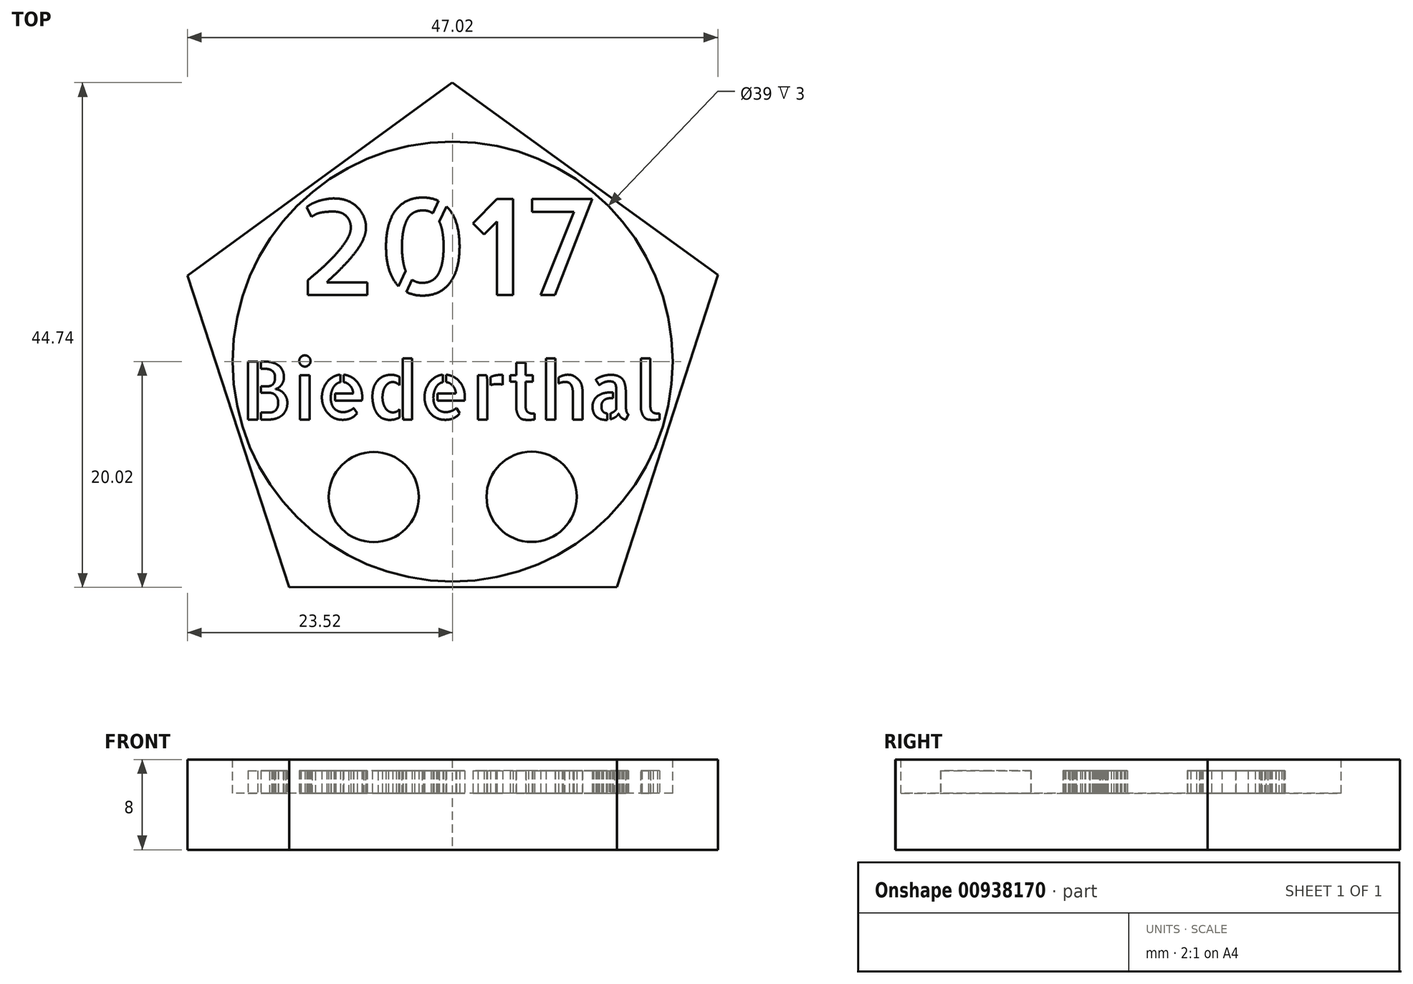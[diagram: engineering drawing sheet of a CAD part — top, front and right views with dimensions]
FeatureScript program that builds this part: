
annotation { "Feature Type Name" : "Feature", "Feature Type Description" : "" }
export const myFeature = defineFeature(function(context is Context, id is Id, definition is map)
    precondition{}
    {
        {
            var Q0;
            Q0=qCreatedBy(makeId("Top.planeOp"),FACE);
            var sketch = newSketch(context, id + "F0", { "sketchPlane" : qUnion([Q0])});
            skCircle(sketch, "E0.cCircle", {"center": v(0, 0) * mm, "radius": 20 * mm, "construction": true});
            skLineSegment(sketch, "E0.0", {"start": v(-23.52, 7.6) * mm, "end": v(-0.04, 24.72) * mm});
            skLineSegment(sketch, "E0.1", {"start": v(-0.04, 24.72) * mm, "end": v(23.5, 7.68) * mm});
            skLineSegment(sketch, "E0.2", {"start": v(23.5, 7.68) * mm, "end": v(14.56, -19.98) * mm});
            skLineSegment(sketch, "E0.3", {"start": v(14.56, -19.98) * mm, "end": v(-14.5, -20.02) * mm});
            skLineSegment(sketch, "E0.4", {"start": v(-14.5, -20.02) * mm, "end": v(-23.52, 7.6) * mm});
            skPoint(sketch, "E0.0.midPoint", {"position": v(-11.78, 16.16) * mm});
            skSolve(sketch);
        }
        {
            var Q0;
            Q0=qSketchRegion(id+"F0",true);
            extrude(context, id + "F1", {"entities" : qUnion([Q0]), "depth" : 8 * mm, "offsetDistance" : 25 * mm});
        }
        {
            var Q0;
            Q0=makeQuery(id+"F1.opExtrude","CAP_FACE",FACE,{"disambiguationData":[OSD([sQuery(id+"F0.wireOp",EDGE,"E0.0"),sQuery(id+"F0.wireOp",EDGE,"E0.1"),sQuery(id+"F0.wireOp",EDGE,"E0.2"),sQuery(id+"F0.wireOp",EDGE,"E0.3"),sQuery(id+"F0.wireOp",EDGE,"E0.4")])],"isStart":false});
            var sketch = newSketch(context, id + "F2", { "sketchPlane" : qUnion([Q0])});
            skCircle(sketch, "E1", {"center": v(0, 0) * mm, "radius": 19.5 * mm});
            skSolve(sketch);
        }
        {
            var Q0;
            {var subQ0=sQuery(id+"F2.wireOp",EDGE,"E1");var subQ4=makeQuery(id+"F2.imprint","INTERSECT",VERTEX,{"derivedFrom":[makeQuery(id+"F1.opExtrude","CAP_EDGE",EDGE,{"disambiguationData":[OSD([sQuery(id+"F0.wireOp",EDGE,"E0.0")])],"isStart":false}),subQ0]});Q0=makeQuery(id+"F2.imprint","IMPRINT",FACE,{"disambiguationData":[TD([[makeQuery(id+"F2.imprint","IMPRINT",EDGE,{"disambiguationData":[TD([[subQ4,1.0]])],"derivedFrom":subQ0}),1.0]])]});}
            extrude(context, id + "F3", {"entities" : qUnion([Q0]), "operationType" : NewBodyOperationType.REMOVE, "oppositeDirection" : true, "depth" : 3 * mm, "offsetDistance" : 25 * mm});
        }
        {
            var Q0;
            Q0=makeQuery(id+"F3.boolean.opBoolean","COPY",FACE,{"derivedFrom":makeQuery(id+"F3.opExtrude","CAP_FACE",FACE,{"disambiguationData":[OSD([sQuery(id+"F2.wireOp",EDGE,"E1")])],"isStart":false})});
            var sketch = newSketch(context, id + "F4", { "sketchPlane" : qUnion([Q0])});
            skText(sketch, "E2", { "text": "2017", "fontName": "AllertaStencil-Regular.ttf"});
            skText(sketch, "E3", { "text": "Biederthal", "fontName": "AllertaStencil-Regular.ttf"});
            skCircle(sketch, "E4", {"center": v(-7, -12.01) * mm, "radius": 4 * mm});
            skCircle(sketch, "E5", {"center": v(7, -11.99) * mm, "radius": 4 * mm});
            const initialGuessF4  = {"E2": [-0.01384, 0.0059, 1, 0, 0.0085], "E3": [-0.0188, -0.00514, 1, 0, 0.00514]};
            skSetInitialGuess(sketch, initialGuessF4);
            skSolve(sketch);
        }
        {
            var Q0;
            Q0=qSketchRegion(id+"F4",true);
            extrude(context, id + "F5", {"entities" : qUnion([Q0]), "operationType" : NewBodyOperationType.ADD, "depth" : 2 * mm, "offsetDistance" : 25 * mm});
        }
    });
